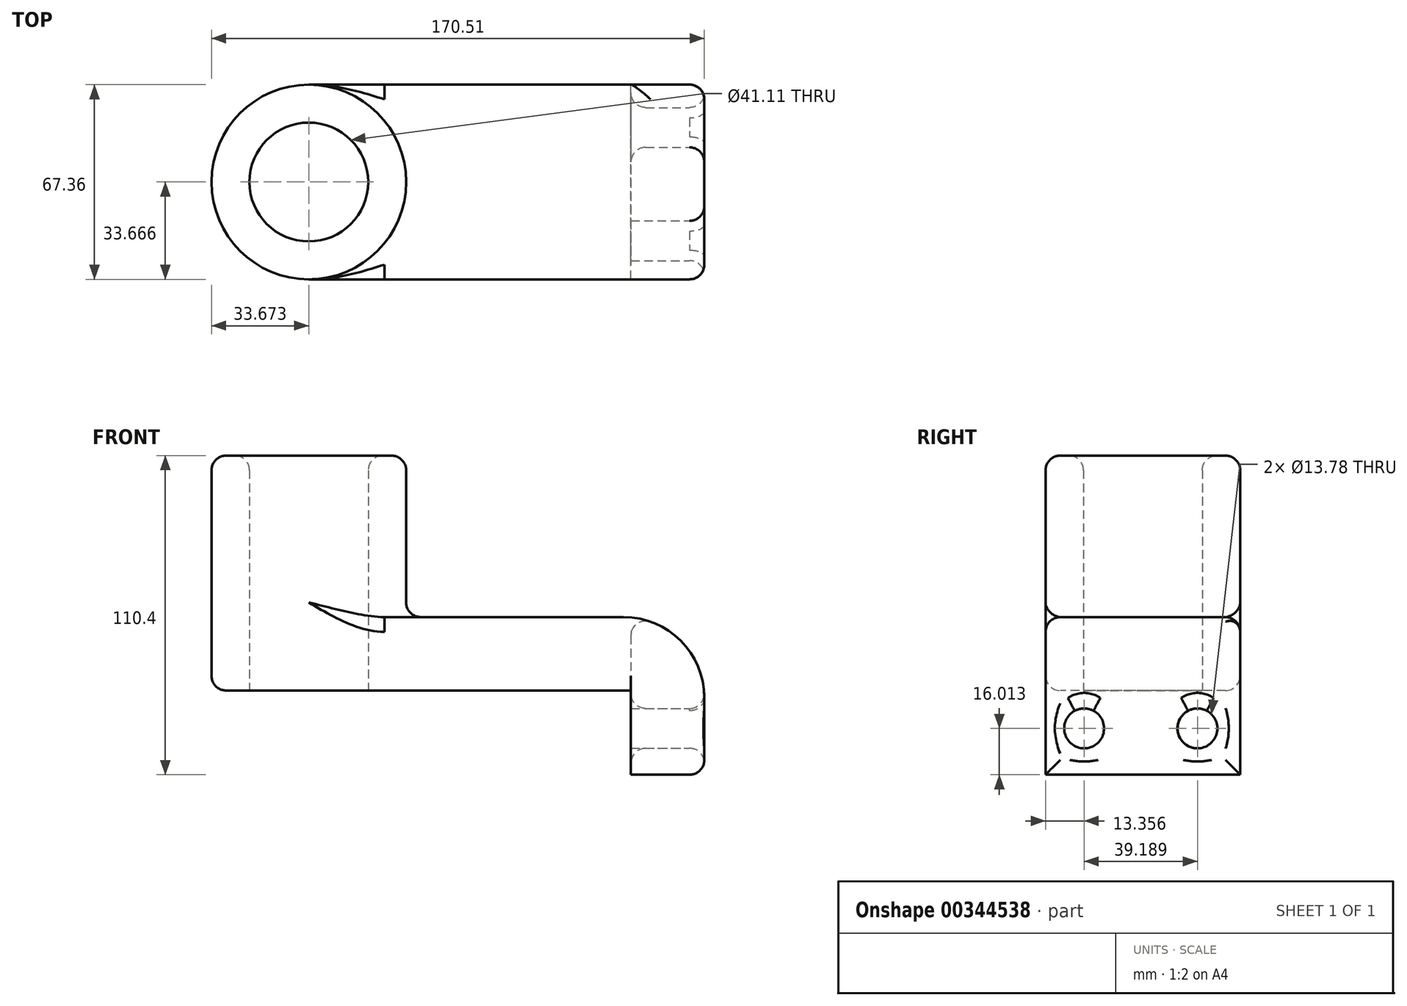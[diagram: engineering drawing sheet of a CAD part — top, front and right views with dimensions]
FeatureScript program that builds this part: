
annotation { "Feature Type Name" : "Feature", "Feature Type Description" : "" }
export const myFeature = defineFeature(function(context is Context, id is Id, definition is map)
    precondition{}
    {
        {
            var Q0;
            Q0=qCreatedBy(makeId("Top.planeOp"),FACE);
            var sketch = newSketch(context, id + "F0", { "sketchPlane" : qUnion([Q0])});
            skLineSegment(sketch, "E0.bottom", {"start": v(-60.54, 34.39) * mm, "end": v(76.3, 34.39) * mm});
            skLineSegment(sketch, "E0.top", {"start": v(-60.54, -32.95) * mm, "end": v(76.3, -32.95) * mm});
            skLineSegment(sketch, "E0.left", {"start": v(-60.54, 34.39) * mm, "end": v(-60.54, -32.95) * mm});
            skLineSegment(sketch, "E0.right", {"start": v(76.3, 34.39) * mm, "end": v(76.3, -32.95) * mm});
            skCircle(sketch, "E1", {"center": v(-60.54, 0.72) * mm, "radius": 33.67 * mm});
            skCircle(sketch, "E2", {"center": v(-60.54, 0.72) * mm, "radius": 20.56 * mm});
            skSolve(sketch);
        }
        {
            var Q0;
            Q0 = qSketchRegion(id + "F0", true);
            extrude(context, id + "F1", {"entities" : qUnion([Q0]), "depth" : 25.4 * mm});
        }
        {
            var Q0;
            {var subQ1=sQuery(id+"F0.wireOp",EDGE,"E0.left");var subQ3=sQuery(id+"F0.wireOp",EDGE,"E2");var subQ4=makeQuery(id+"F0.imprint","INTERSECT",VERTEX,{"disambiguationData":[OD(0.0)],"derivedFrom":[subQ1,subQ3]});Q0=makeQuery(id+"F0.imprint","IMPRINT",FACE,{"disambiguationData":[TD([[makeQuery(id+"F0.imprint","IMPRINT",EDGE,{"disambiguationData":[TD([[subQ4,-1.0]])],"derivedFrom":subQ3}),-1.0]])]});}
            var Q1;
            {var subQ1=sQuery(id+"F0.wireOp",EDGE,"E0.left");var subQ3=sQuery(id+"F0.wireOp",EDGE,"E2");var subQ4=makeQuery(id+"F0.imprint","INTERSECT",VERTEX,{"disambiguationData":[OD(0.0)],"derivedFrom":[subQ1,subQ3]});Q1=makeQuery(id+"F0.imprint","IMPRINT",FACE,{"disambiguationData":[TD([[makeQuery(id+"F0.imprint","IMPRINT",EDGE,{"disambiguationData":[TD([[subQ4,1.0]])],"derivedFrom":subQ3}),-1.0]])]});}
            extrude(context, id + "F2", {"entities" : qUnion([Q0, Q1]), "operationType" : NewBodyOperationType.ADD, "depth" : 81.28 * mm});
        }
        {
            var Q0;
            Q0=makeQuery(id+"F1.opExtrude","SWEPT_FACE",FACE,{"disambiguationData":[OSD([sQuery(id+"F0.wireOp",EDGE,"E0.right")])]});
            var sketch = newSketch(context, id + "F3", { "sketchPlane" : qUnion([Q0])});
            skLineSegment(sketch, "E3.bottom", {"start": v(-32.95, 25.4) * mm, "end": v(34.39, 25.4) * mm});
            skLineSegment(sketch, "E3.top", {"start": v(-32.95, 25.4) * mm, "end": v(34.39, 25.4) * mm});
            skLineSegment(sketch, "E4.bottom", {"start": v(-32.95, 25.4) * mm, "end": v(34.4, 25.4) * mm});
            skLineSegment(sketch, "E4.top", {"start": v(-32.95, -29.12) * mm, "end": v(34.4, -29.12) * mm});
            skLineSegment(sketch, "E4.left", {"start": v(-32.95, 25.4) * mm, "end": v(-32.95, -29.12) * mm});
            skLineSegment(sketch, "E4.right", {"start": v(34.4, 25.4) * mm, "end": v(34.4, -29.12) * mm});
            skCircle(sketch, "E5", {"center": v(-19.6, -13.1) * mm, "radius": 6.9 * mm});
            skCircle(sketch, "E6.MirrorC", {"center": v(19.6, -13.1) * mm, "radius": 6.9 * mm});
            skSolve(sketch);
        }
        {
            var Q0;
            {var subQ4=sQuery(id+"F3.wireOp",EDGE,"E4.top");Q0=makeQuery(id+"F3.imprint","IMPRINT",FACE,{"disambiguationData":[TD([[makeQuery(id+"F3.imprint","IMPRINT",EDGE,{"derivedFrom":subQ4}),1.0]])]});}
            extrude(context, id + "F4", {"entities" : qUnion([Q0]), "operationType" : NewBodyOperationType.ADD, "depth" : -25.4 * mm});
        }
        {
            var Q0;
            {var subQ0=sQuery(id+"F0.wireOp",EDGE,"E1");Q0=makeQuery(id+"F2.boolean.opBoolean","MERGE",FACE,{"derivedFrom":[makeQuery(id+"F1.opExtrude","SWEPT_FACE",FACE,{"disambiguationData":[OSD([subQ0])]}),makeQuery(id+"F2.opExtrude","SWEPT_FACE",FACE,{"disambiguationData":[OSD([subQ0])]})]});}
            fillet(context, id + "F5", {"entities" : qUnion([Q0]), "radius" : 5.08 * mm, "tangentPropagation" : true, "allowEdgeOverflow" : false});
        }
        {
            var Q0;
            Q0=makeQuery(id+"F4.boolean.opBoolean","MERGE",EDGE,{"derivedFrom":[makeQuery(id+"F1.opExtrude","CAP_EDGE",EDGE,{"disambiguationData":[OSD([sQuery(id+"F0.wireOp",EDGE,"E0.right")])],"isStart":false}),makeQuery(id+"F4.opExtrude","CAP_EDGE",EDGE,{"disambiguationData":[OSD([sQuery(id+"F3.wireOp",EDGE,"E4.bottom")])],"isStart":true})]});
            fillet(context, id + "F6", {"entities" : qUnion([Q0]), "radius" : 27.94 * mm, "tangentPropagation" : true, "allowEdgeOverflow" : false});
        }
        {
            var Q0;
            Q0=makeQuery(id+"F2.opExtrude","CAP_EDGE",EDGE,{"disambiguationData":[OSD([sQuery(id+"F0.wireOp",EDGE,"E2")])],"isStart":false});
            var Q1;
            Q1=makeQuery(id+"F4.opExtrude","CAP_EDGE",EDGE,{"disambiguationData":[OSD([sQuery(id+"F3.wireOp",EDGE,"E4.top")])],"isStart":true});
            var Q2;
            Q2=makeQuery(id+"F4.opExtrude","CAP_EDGE",EDGE,{"disambiguationData":[OSD([sQuery(id+"F3.wireOp",EDGE,"E4.right")])],"isStart":true});
            var Q3;
            {var subQ0=sQuery(id+"F0.wireOp",EDGE,"E0.right");Q3=makeQuery(id+"F4.boolean.opBoolean","MERGE",FACE,{"derivedFrom":[makeQuery(id+"F1.opExtrude","SWEPT_FACE",FACE,{"disambiguationData":[OSD([subQ0])]}),makeQuery(id+"F4.opExtrude","CAP_FACE",FACE,{"disambiguationData":[OSD([sQuery(id+"F0.wireOp",EDGE,"E0.bottom"),subQ0,sQuery(id+"F3.wireOp",EDGE,"E4.bottom"),sQuery(id+"F3.wireOp",EDGE,"E4.top"),sQuery(id+"F3.wireOp",EDGE,"E4.left"),sQuery(id+"F3.wireOp",EDGE,"E4.right"),sQuery(id+"F3.wireOp",EDGE,"E5"),sQuery(id+"F3.wireOp",EDGE,"E6.MirrorC")])],"isStart":true})]});}
            var Q4;
            Q4=makeQuery(id+"F4.opExtrude","SWEPT_FACE",FACE,{"disambiguationData":[OSD([sQuery(id+"F3.wireOp",EDGE,"E6.MirrorC")])]});
            var Q5;
            {var subQ0=sQuery(id+"F3.wireOp",EDGE,"E4.bottom");var subQ1=sQuery(id+"F0.wireOp",EDGE,"E0.right");Q5=makeQuery(id+"F6.opFillet","BLEND_EDGE",EDGE,{"blendedFrom":[makeQuery(id+"F4.boolean.opBoolean","MERGE",EDGE,{"derivedFrom":[makeQuery(id+"F1.opExtrude","CAP_EDGE",EDGE,{"disambiguationData":[OSD([subQ1])],"isStart":false}),makeQuery(id+"F4.opExtrude","CAP_EDGE",EDGE,{"disambiguationData":[OSD([subQ0])],"isStart":true})]}),makeQuery(id+"F4.boolean.opBoolean","MERGE",FACE,{"derivedFrom":[makeQuery(id+"F1.opExtrude","SWEPT_FACE",FACE,{"disambiguationData":[OSD([subQ1])]}),makeQuery(id+"F4.opExtrude","CAP_FACE",FACE,{"disambiguationData":[OSD([sQuery(id+"F0.wireOp",EDGE,"E0.bottom"),subQ1,subQ0,sQuery(id+"F3.wireOp",EDGE,"E4.top"),sQuery(id+"F3.wireOp",EDGE,"E4.left"),sQuery(id+"F3.wireOp",EDGE,"E4.right"),sQuery(id+"F3.wireOp",EDGE,"E5"),sQuery(id+"F3.wireOp",EDGE,"E6.MirrorC")])],"isStart":true})]})],"blendedInto":[makeQuery(id+"F4.boolean.opBoolean","MERGE",FACE,{"derivedFrom":[makeQuery(id+"F1.opExtrude","SWEPT_FACE",FACE,{"disambiguationData":[OSD([subQ1])]}),makeQuery(id+"F4.opExtrude","CAP_FACE",FACE,{"disambiguationData":[OSD([sQuery(id+"F0.wireOp",EDGE,"E0.bottom"),subQ1,subQ0,sQuery(id+"F3.wireOp",EDGE,"E4.top"),sQuery(id+"F3.wireOp",EDGE,"E4.left"),sQuery(id+"F3.wireOp",EDGE,"E4.right"),sQuery(id+"F3.wireOp",EDGE,"E5"),sQuery(id+"F3.wireOp",EDGE,"E6.MirrorC")])],"isStart":true})]})]});}
            var Q6;
            Q6=makeQuery(id+"F6.opFillet","BLEND_FACE",FACE,{"disambiguationData":[OSD([sQuery(id+"F0.wireOp",EDGE,"E0.right"),sQuery(id+"F3.wireOp",EDGE,"E4.bottom")])]});
            fillet(context, id + "F7", {"entities" : qUnion([Q0, Q1, Q2, Q3, Q4, Q5, Q6]), "radius" : 5.08 * mm, "tangentPropagation" : true, "allowEdgeOverflow" : false});
        }
    });
